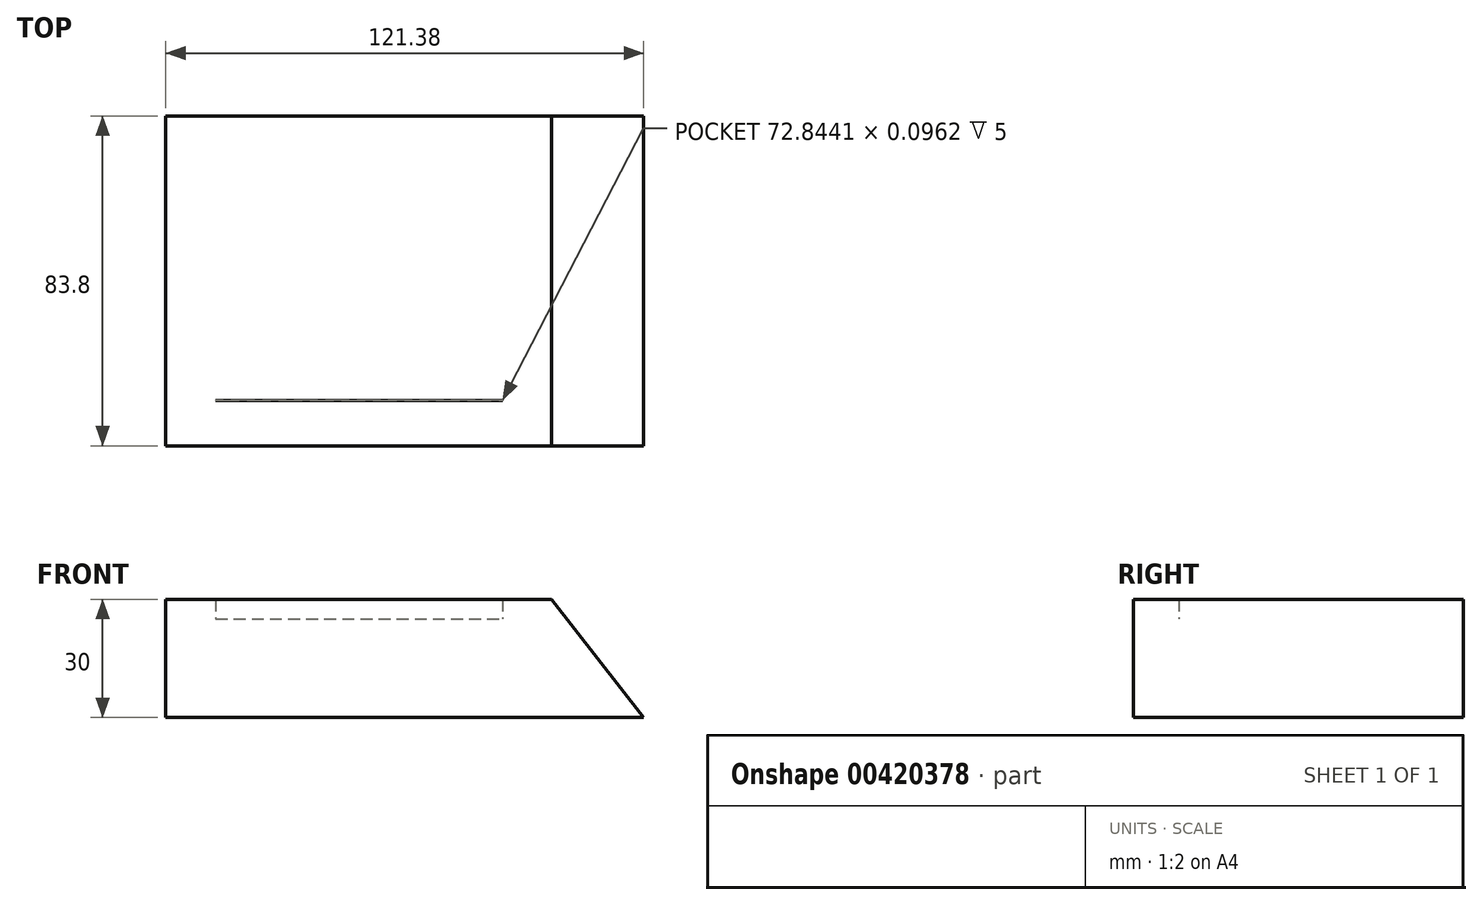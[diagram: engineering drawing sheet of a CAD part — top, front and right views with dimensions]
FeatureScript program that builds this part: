
annotation { "Feature Type Name" : "Feature", "Feature Type Description" : "" }
export const myFeature = defineFeature(function(context is Context, id is Id, definition is map)
    precondition{}
    {
        {
            var Q0;
            Q0=qCreatedBy(makeId("Top.planeOp"),FACE);
            var sketch = newSketch(context, id + "F0", { "sketchPlane" : qUnion([Q0])});
            skLineSegment(sketch, "E0.bottom", {"start": v(60.69, -41.9) * mm, "end": v(-60.69, -41.9) * mm});
            skLineSegment(sketch, "E0.top", {"start": v(60.69, 41.9) * mm, "end": v(-60.69, 41.9) * mm});
            skLineSegment(sketch, "E0.left", {"start": v(60.69, -41.9) * mm, "end": v(60.69, 41.9) * mm});
            skLineSegment(sketch, "E0.right", {"start": v(-60.69, -41.9) * mm, "end": v(-60.69, 41.9) * mm});
            skPoint(sketch, "E0.middle", {"position": v(0, 0) * mm});
            skSolve(sketch);
        }
        {
            var Q0;
            Q0 = qSketchRegion(id + "F0", true);
            extrude(context, id + "F1", {"entities" : qUnion([Q0]), "depth" : 30 * mm});
        }
        {
            var Q0;
            Q0=qCreatedBy(makeId("Front.planeOp"),FACE);
            var sketch = newSketch(context, id + "F2", { "sketchPlane" : qUnion([Q0])});
            skLineSegment(sketch, "E1", {"start": v(60.74, 0) * mm, "end": v(37.3, 30) * mm});
            skLineSegment(sketch, "E2", {"start": v(37.3, 30) * mm, "end": v(60.69, 30) * mm});
            skLineSegment(sketch, "E3", {"start": v(60.69, 30) * mm, "end": v(60.69, 0) * mm});
            skLineSegment(sketch, "E4", {"start": v(60.74, 0) * mm, "end": v(60.69, 0) * mm});
            skSolve(sketch);
        }
        {
            var Q0;
            Q0 = qSketchRegion(id + "F2", true);
            extrude(context, id + "F3", {"entities" : qUnion([Q0]), "operationType" : NewBodyOperationType.REMOVE, "endBound" : BoundingType.SYMMETRIC, "oppositeDirection" : true, "depth" : 500 * mm});
        }
        {
            var Q0;
            Q0=makeQuery(id+"F1.opExtrude","CAP_FACE",FACE,{"disambiguationData":[OSD([sQuery(id+"F0.wireOp",EDGE,"E0.bottom"),sQuery(id+"F0.wireOp",EDGE,"E0.top"),sQuery(id+"F0.wireOp",EDGE,"E0.left"),sQuery(id+"F0.wireOp",EDGE,"E0.right")])],"isStart":false});
            var sketch = newSketch(context, id + "F4", { "sketchPlane" : qUnion([Q0])});
            skLineSegment(sketch, "E5.bottom", {"start": v(-52.98, 35.88) * mm, "end": v(29.86, 35.88) * mm});
            skLineSegment(sketch, "E5.top", {"start": v(-52.98, -35.4) * mm, "end": v(29.86, -35.4) * mm});
            skLineSegment(sketch, "E5.left", {"start": v(-52.98, 35.88) * mm, "end": v(-52.98, -35.4) * mm});
            skLineSegment(sketch, "E5.right", {"start": v(29.86, 35.88) * mm, "end": v(29.86, -35.4) * mm});
            skSolve(sketch);
        }
        {
            var Q0;
            Q0 = qSketchRegion(id + "F4", true);
            extrude(context, id + "F5", {"entities" : qUnion([Q0]), "operationType" : NewBodyOperationType.REMOVE, "oppositeDirection" : true, "depth" : 5 * mm});
        }
        {
            var Q0;
            Q0=makeQuery(id+"F5.boolean.opBoolean","COPY",FACE,{"derivedFrom":makeQuery(id+"F5.opExtrude","CAP_FACE",FACE,{"disambiguationData":[OSD([sQuery(id+"F4.wireOp",EDGE,"E5.bottom"),sQuery(id+"F4.wireOp",EDGE,"E5.top"),sQuery(id+"F4.wireOp",EDGE,"E5.left"),sQuery(id+"F4.wireOp",EDGE,"E5.right")])],"isStart":false})});
            var sketch = newSketch(context, id + "F6", { "sketchPlane" : qUnion([Q0])});
            skLineSegment(sketch, "E6.bottom", {"start": v(-52.98, 35.88) * mm, "end": v(29.86, 35.88) * mm});
            skLineSegment(sketch, "E6.top", {"start": v(-52.98, -35.4) * mm, "end": v(29.86, -35.4) * mm});
            skLineSegment(sketch, "E6.left", {"start": v(-52.98, 35.88) * mm, "end": v(-52.98, -35.4) * mm});
            skLineSegment(sketch, "E6.right", {"start": v(29.86, 35.88) * mm, "end": v(29.86, -35.4) * mm});
            skLineSegment(sketch, "E7.0", {"start": v(-47.98, 30.88) * mm, "end": v(24.86, 30.88) * mm});
            skLineSegment(sketch, "E7.1", {"start": v(-47.98, 30.88) * mm, "end": v(-47.98, -30.4) * mm});
            skLineSegment(sketch, "E7.2", {"start": v(-47.98, -30.4) * mm, "end": v(24.86, -30.4) * mm});
            skLineSegment(sketch, "E7.3", {"start": v(24.86, 30.88) * mm, "end": v(24.86, -30.4) * mm});
            skSolve(sketch);
        }
        {
            var Q0;
            Q0 = qSketchRegion(id + "F6", true);
            extrude(context, id + "F7", {"entities" : qUnion([Q0]), "operationType" : NewBodyOperationType.REMOVE, "oppositeDirection" : true, "depth" : 10 * mm});
        }
        {
            var Q0;
            Q0=makeQuery(id+"F7.boolean.opBoolean","COPY",FACE,{"derivedFrom":makeQuery(id+"F7.opExtrude","CAP_FACE",FACE,{"disambiguationData":[OSD([sQuery(id+"F6.wireOp",EDGE,"E6.bottom"),sQuery(id+"F6.wireOp",EDGE,"E6.top"),sQuery(id+"F6.wireOp",EDGE,"E6.left"),sQuery(id+"F6.wireOp",EDGE,"E6.right"),sQuery(id+"F6.wireOp",EDGE,"E7.0"),sQuery(id+"F6.wireOp",EDGE,"E7.1"),sQuery(id+"F6.wireOp",EDGE,"E7.2"),sQuery(id+"F6.wireOp",EDGE,"E7.3")])],"isStart":false})});
            var sketch = newSketch(context, id + "F8", { "sketchPlane" : qUnion([Q0])});
            skLineSegment(sketch, "E8.0.0", {"start": v(29.86, 35.88) * mm, "end": v(-52.98, 35.88) * mm});
            skLineSegment(sketch, "E8.0.1", {"start": v(-52.98, 35.88) * mm, "end": v(-52.98, -35.4) * mm});
            skLineSegment(sketch, "E8.0.2", {"start": v(-52.98, -35.4) * mm, "end": v(29.86, -35.4) * mm});
            skLineSegment(sketch, "E8.0.3", {"start": v(29.86, -35.4) * mm, "end": v(29.86, 35.88) * mm});
            skLineSegment(sketch, "E9.0", {"start": v(-47.98, 30.88) * mm, "end": v(24.86, 30.88) * mm});
            skLineSegment(sketch, "E10.0", {"start": v(-47.98, 30.88) * mm, "end": v(-47.98, -30.4) * mm});
            skLineSegment(sketch, "E11.0", {"start": v(24.86, 30.88) * mm, "end": v(24.86, -30.4) * mm});
            skLineSegment(sketch, "E12.0", {"start": v(-47.98, -30.4) * mm, "end": v(24.86, -30.4) * mm});
            skSolve(sketch);
        }
        {
            var Q0;
            Q0 = qSketchRegion(id + "F8", true);
            var Q1;
            Q1=makeQuery(id+"F1.opExtrude","CAP_FACE",FACE,{"disambiguationData":[OSD([sQuery(id+"F0.wireOp",EDGE,"E0.bottom"),sQuery(id+"F0.wireOp",EDGE,"E0.top"),sQuery(id+"F0.wireOp",EDGE,"E0.left"),sQuery(id+"F0.wireOp",EDGE,"E0.right")])],"isStart":false});
            extrude(context, id + "F9", {"entities" : qUnion([Q0]), "endBound" : BoundingType.UP_TO_SURFACE, "endBoundEntityFace" : qUnion([Q1]), "depth" : 25 * mm});
        }
        {
            var Q0;
            Q0=makeQuery(id+"F9.opExtrude","CAP_FACE",FACE,{"disambiguationData":[OSD([sQuery(id+"F8.wireOp",EDGE,"E8.0.0"),sQuery(id+"F8.wireOp",EDGE,"E8.0.1"),sQuery(id+"F8.wireOp",EDGE,"E8.0.2"),sQuery(id+"F8.wireOp",EDGE,"E8.0.3"),sQuery(id+"F8.wireOp",EDGE,"E9.0"),sQuery(id+"F8.wireOp",EDGE,"E10.0"),sQuery(id+"F8.wireOp",EDGE,"E11.0"),sQuery(id+"F8.wireOp",EDGE,"E12.0")])],"isStart":false});
            var sketch = newSketch(context, id + "F10", { "sketchPlane" : qUnion([Q0])});
            skLineSegment(sketch, "E13.bottom", {"start": v(-49.16, 32.82) * mm, "end": v(26.8, 32.82) * mm});
            skLineSegment(sketch, "E13.top", {"start": v(-49.16, -30.3) * mm, "end": v(26.8, -30.3) * mm});
            skLineSegment(sketch, "E13.left", {"start": v(-49.16, 32.82) * mm, "end": v(-49.16, -30.3) * mm});
            skLineSegment(sketch, "E13.right", {"start": v(26.8, 32.82) * mm, "end": v(26.8, -30.3) * mm});
            skSolve(sketch);
        }
        {
            var Q0;
            Q0 = qSketchRegion(id + "F10", true);
            var Q1;
            Q1=makeQuery(id+"F5.boolean.opBoolean","COPY",FACE,{"derivedFrom":makeQuery(id+"F5.opExtrude","CAP_FACE",FACE,{"disambiguationData":[OSD([sQuery(id+"F4.wireOp",EDGE,"E5.bottom"),sQuery(id+"F4.wireOp",EDGE,"E5.top"),sQuery(id+"F4.wireOp",EDGE,"E5.left"),sQuery(id+"F4.wireOp",EDGE,"E5.right")])],"isStart":false})});
            extrude(context, id + "F11", {"entities" : qUnion([Q0]), "operationType" : NewBodyOperationType.ADD, "endBound" : BoundingType.UP_TO_SURFACE, "oppositeDirection" : true, "endBoundEntityFace" : qUnion([Q1]), "depth" : 25 * mm});
        }
    });
